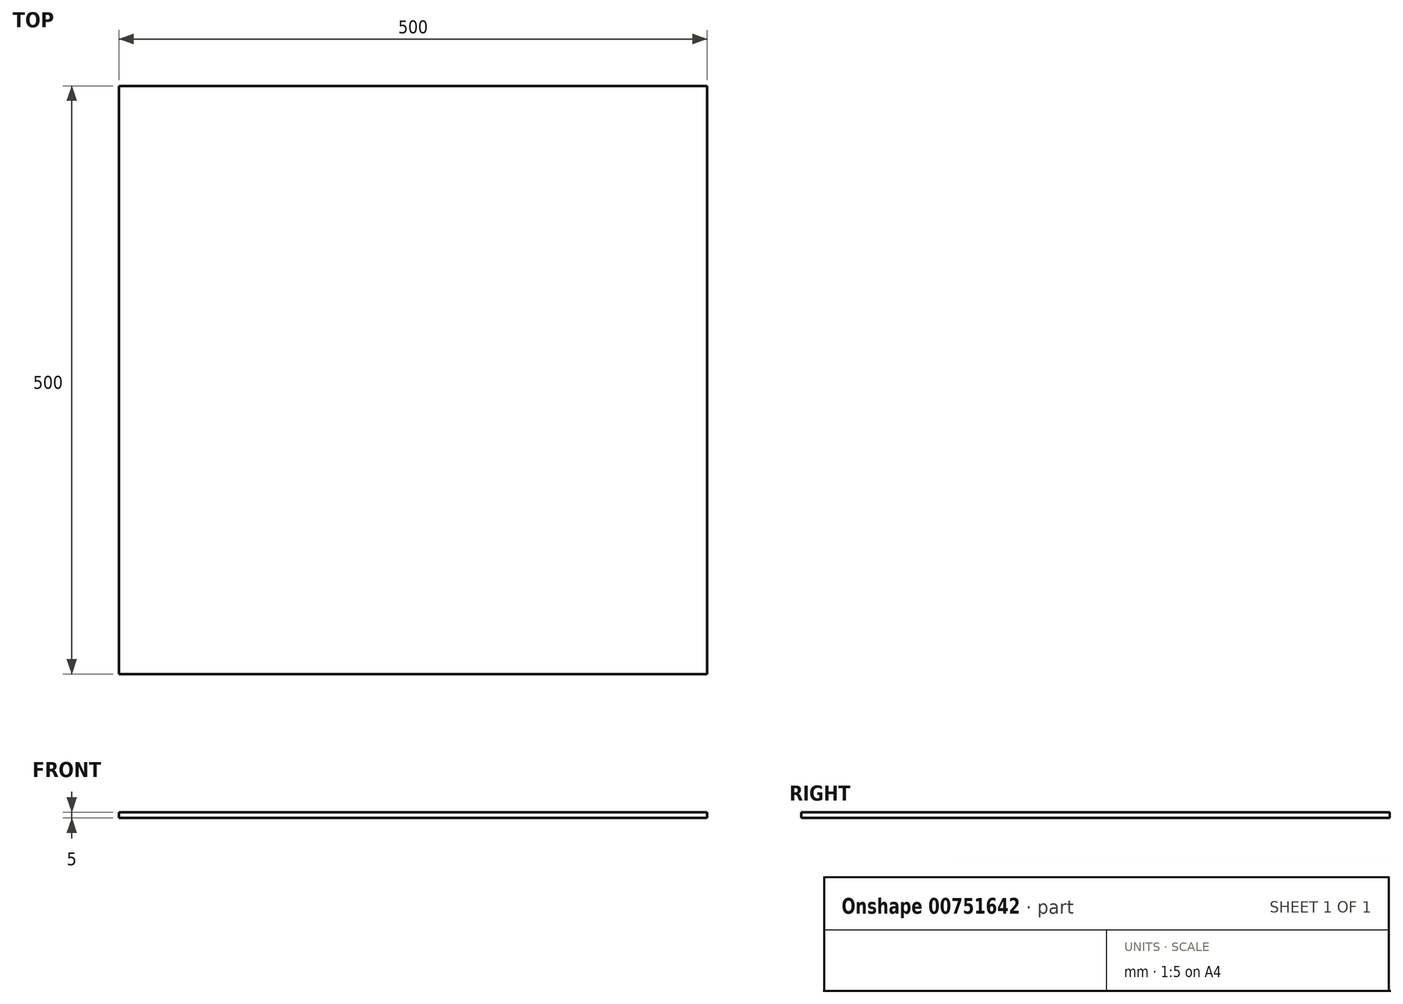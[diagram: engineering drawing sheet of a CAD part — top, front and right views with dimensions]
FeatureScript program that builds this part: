
annotation { "Feature Type Name" : "Feature", "Feature Type Description" : "" }
export const myFeature = defineFeature(function(context is Context, id is Id, definition is map)
    precondition{}
    {
        {
            var Q0;
            Q0=qCreatedBy(makeId("Top.planeOp"),FACE);
            var sketch = newSketch(context, id + "F0", { "sketchPlane" : qUnion([Q0])});
            skLineSegment(sketch, "E0.bottom", {"start": v(0, 0) * mm, "end": v(500, 0) * mm});
            skLineSegment(sketch, "E0.top", {"start": v(0, 500) * mm, "end": v(500, 500) * mm});
            skLineSegment(sketch, "E0.left", {"start": v(0, 0) * mm, "end": v(0, 500) * mm});
            skLineSegment(sketch, "E0.right", {"start": v(500, 0) * mm, "end": v(500, 500) * mm});
            skSolve(sketch);
        }
        {
            var Q0;
            Q0=qSketchRegion(id+"F0",true);
            extrude(context, id + "F1", {"entities" : qUnion([Q0]), "depth" : 5 * mm});
        }
    });
